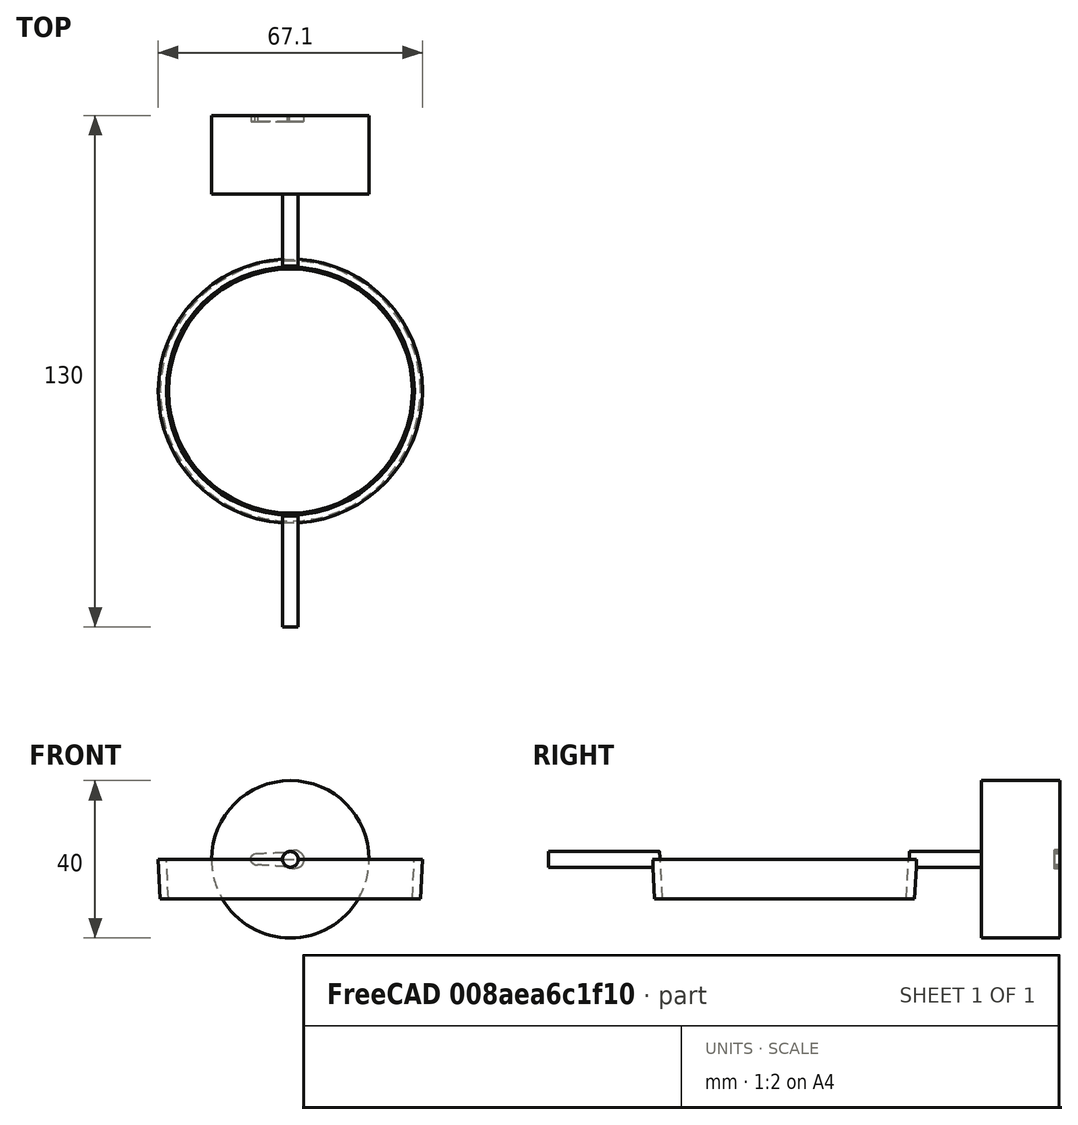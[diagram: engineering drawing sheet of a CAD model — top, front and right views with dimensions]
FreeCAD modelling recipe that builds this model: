
FCSTD DOCUMENT  (FreeCAD 0.20R29177 +233 (Git))
Label: proyecto-cupholder-1-anillo
License: Creative Commons Attribution-ShareAlike
LicenseURL: http://creativecommons.org/licenses/by-sa/4.0/
objects: Part::Cylinder×4, Part::Cut×3, Part::MultiFuse×2, Sketcher::SketchObject×1, PartDesign::Revolution×1, PartDesign::Body×1, Part::Feature×1, Part::Extrusion×1
note: 15 computed .brp shape members not serialized (recipe doc carries the construction recipe); baked Part::Feature solids carry a one-line shape summary decoded from their .brp

FEATURE [Sketcher::SketchObject] Sketch
  FullyConstrained = true
  MapMode = 5
  Placement = pos=(0,0,0) rot=(1,0,0;1.5708rad)
  Support = -> [XZ_Plane]
  sketch-geometry (6):
    g0: LineSegment StartX=0 StartY=1 StartZ=0 EndX=34 EndY=1 EndZ=0
    g1: LineSegment StartX=34 StartY=1 StartZ=0 EndX=40 EndY=70 EndZ=0
    g2: LineSegment StartX=40 StartY=70 StartZ=0 EndX=44.087 EndY=70 EndZ=0
    g3: LineSegment StartX=44.087 StartY=70 StartZ=0 EndX=38 EndY=0 EndZ=0
    g4: LineSegment StartX=38 StartY=0 StartZ=0 EndX=0 EndY=0 EndZ=0
    g5: LineSegment StartX=0 StartY=0 StartZ=0 EndX=0 EndY=1 EndZ=0
  constraints (17):
    c: PointOnObject(g0,g-2)
    c: Horizontal(g0)
    c: Coincident(g0,g1)
    c: Coincident(g1,g2)
    c: Horizontal(g2)
    c: Coincident(g2,g3)
    c: Coincident(g3,g4)
    c: Horizontal(g4)
    c: Coincident(g4,g5)
    c: Coincident(g5,g0)
    c: DistanceY(g5,g5) = 1
    c: Coincident(g4,g-1)
    c: DistanceX(g0,g0) = 34
    c: DistanceX(g4,g4) = 38
    c: Parallel(g1,g3)
    c: DistanceX(g-1,g1) = 40
    c: DistanceY(g-1,g2) = 70
FEATURE [PartDesign::Revolution] Revolution
  Angle = 360
  Axis = (0,-2e-16,1)
  Base = (0,0,0)
  Placement = pos=(0,0,0) rot=(1,0,0;1.5708rad)
  Profile = -> Sketch
  ReferenceAxis = -> Sketch [V_Axis]
  Refine = true
  Reversed = true
FEATURE [PartDesign::Body] Body  label="vaso"
  Group = -> [Sketch,Revolution]
  Origin = -> Origin
  Tip = -> Revolution
FEATURE [Part::Cylinder] Cylinder003
  Angle = 360
  AttacherType = Attacher::AttachEngine3D
  FirstAngle = 0
  Height = 120
  Placement = pos=(0,60,70) rot=(1,0,0;1.5708rad)
  Radius = 4
  SecondAngle = 0
FEATURE [Part::Cylinder] Cylinder004
  Angle = 360
  AttacherType = Attacher::AttachEngine3D
  FirstAngle = 0
  Height = 30
  Placement = pos=(0,0,56) rot=(0,0,1;0rad)
  Radius = 31.75
  SecondAngle = 0
FEATURE [Part::Cut] Cut001
  Base = -> Cylinder003
  Refine = true
  Tool = -> Cylinder004
FEATURE [Part::Cylinder] Cylinder005
  Angle = 360
  AttacherType = Attacher::AttachEngine3D
  FirstAngle = 0
  Height = 20
  Placement = pos=(0,70,70) rot=(1,0,0;1.5708rad)
  Radius = 20
  SecondAngle = 0
FEATURE [Part::MultiFuse] Fusion  label="eje"
  Refine = true
  Shapes = -> [Cylinder005,Cut001]
FEATURE [Part::MultiFuse] Fusion001  label="estructura"
  Refine = true
  Shapes = -> [Fusion,Body]
FEATURE [Part::Feature] path2399
  shape: bbox 13.5 x 4.857 x 2e-07 mm, 0 faces, 0 solids (baked)
FEATURE [Part::Extrusion] Extrude  label="corona_servo"
  Base = -> path2399
  Dir = (0,0,1)
  DirMode = 2
  FaceMakerClass = Part::FaceMakerBullseye
  LengthFwd = 4.5
  LengthRev = 0
  Placement = pos=(-12,73,75) rot=(1,0,0;1.5708rad)
  Solid = true
  Symmetric = false
FEATURE [Part::Cut] Cut
  Base = -> Fusion001
  Refine = true
  Tool = -> Extrude
FEATURE [Part::Cylinder] Cylinder
  Angle = 360
  AttacherType = Attacher::AttachEngine3D
  FirstAngle = 0
  Height = 60
  Radius = 40
  SecondAngle = 0
FEATURE [Part::Cut] Cut002
  Base = -> Cut
  Refine = true
  Tool = -> Cylinder
